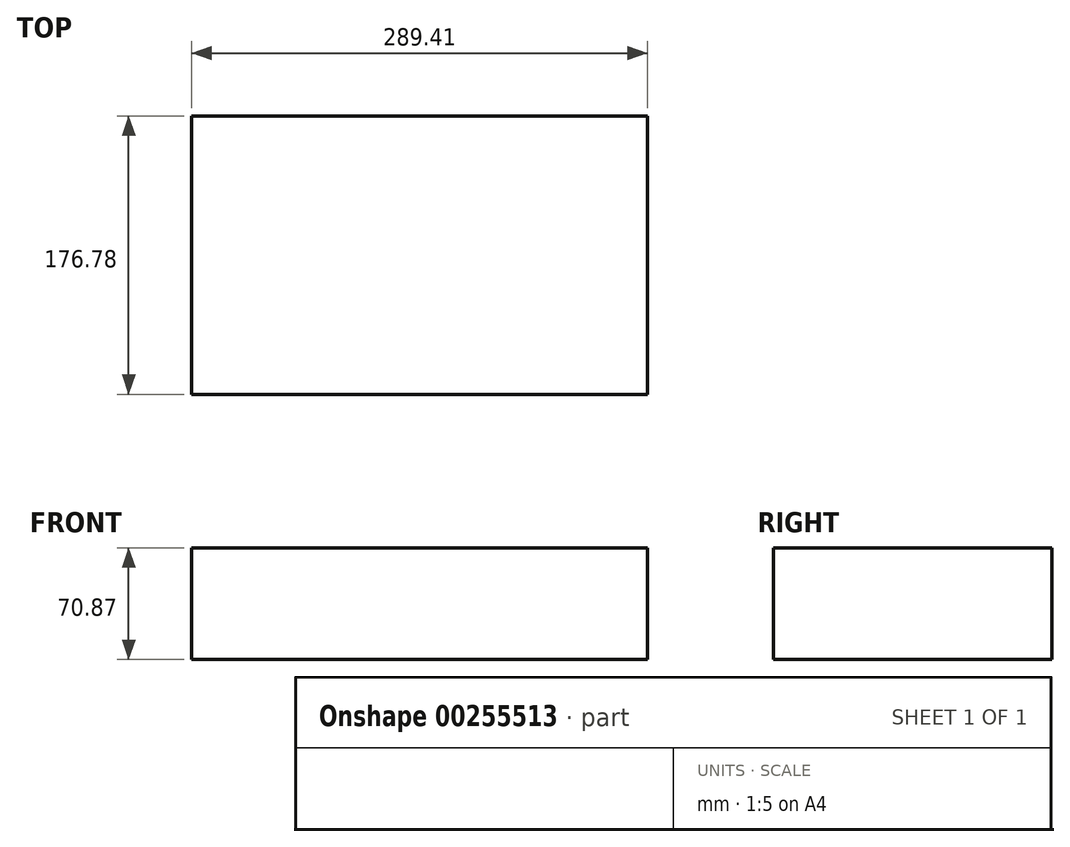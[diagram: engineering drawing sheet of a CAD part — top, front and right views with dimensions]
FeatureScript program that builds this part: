
annotation { "Feature Type Name" : "Feature", "Feature Type Description" : "" }
export const myFeature = defineFeature(function(context is Context, id is Id, definition is map)
    precondition{}
    {
        {
            var Q0;
            Q0=qCreatedBy(makeId("Top.planeOp"),FACE);
            var sketch = newSketch(context, id + "F0", { "sketchPlane" : qUnion([Q0])});
            skLineSegment(sketch, "E0.bottom", {"start": v(-148.6, 102.88) * mm, "end": v(140.81, 102.88) * mm});
            skLineSegment(sketch, "E0.top", {"start": v(-148.6, -73.9) * mm, "end": v(140.81, -73.9) * mm});
            skLineSegment(sketch, "E0.left", {"start": v(-148.6, 102.88) * mm, "end": v(-148.6, -73.9) * mm});
            skLineSegment(sketch, "E0.right", {"start": v(140.81, 102.88) * mm, "end": v(140.81, -73.9) * mm});
            skSolve(sketch);
        }
        {
            var Q0;
            Q0=makeQuery(id+"F0.imprint","IMPRINT",FACE,{"disambiguationData":[TD([[makeQuery(id+"F0.imprint","IMPRINT",EDGE,{"derivedFrom":sQuery(id+"F0.wireOp",EDGE,"E0.bottom")}),-1.0]])]});
            extrude(context, id + "F1", {"entities" : qUnion([Q0]), "depth" : 70.87 * mm});
        }
    });
